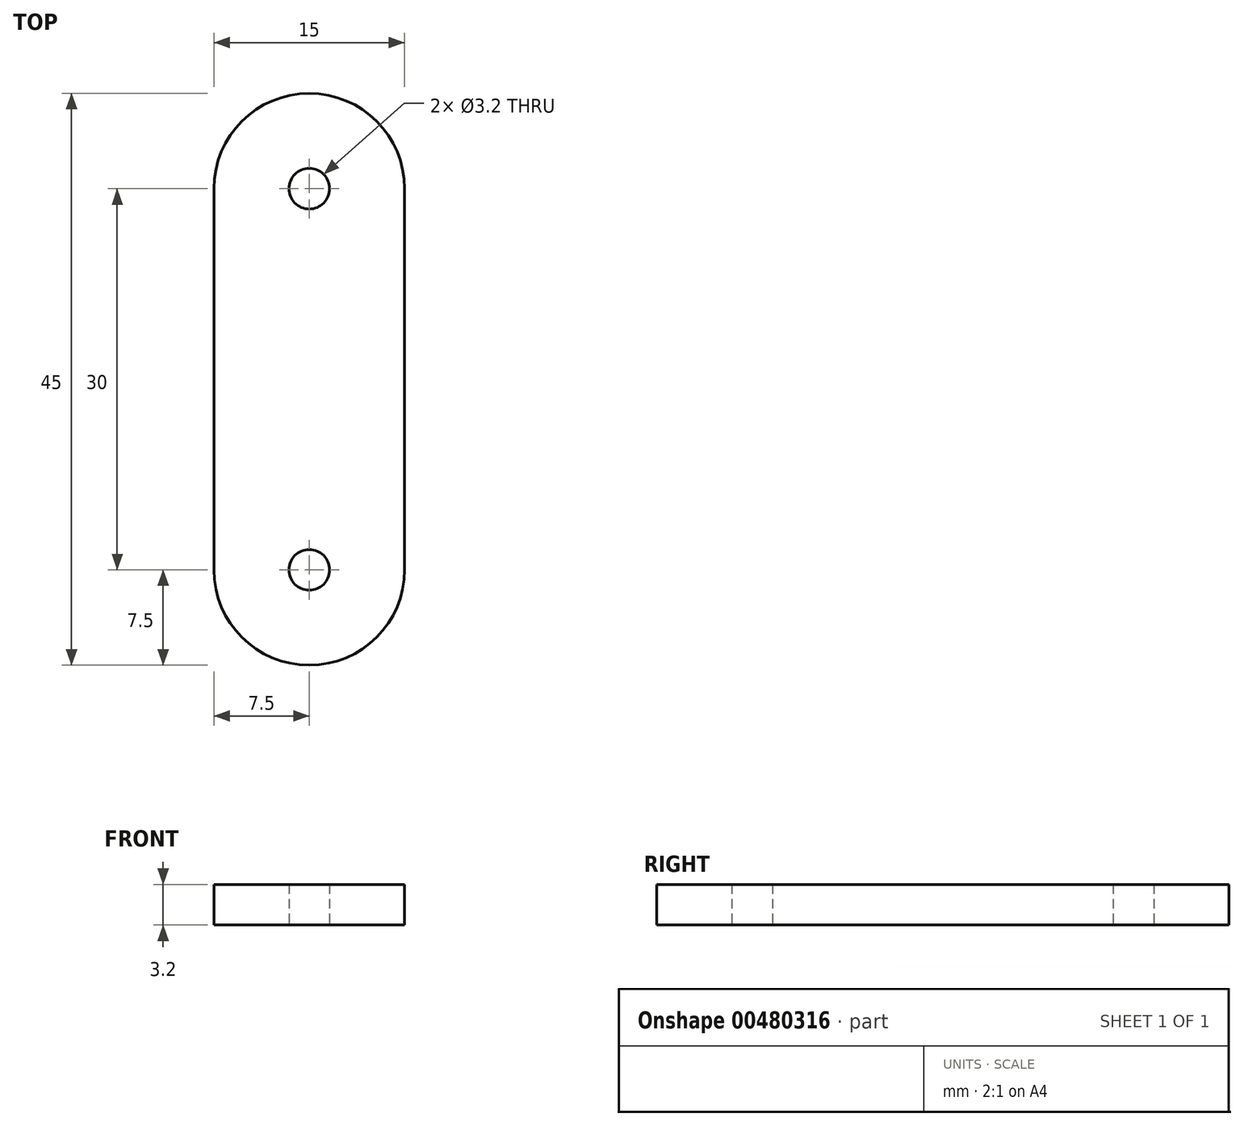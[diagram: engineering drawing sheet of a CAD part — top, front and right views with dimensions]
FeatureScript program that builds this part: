
annotation { "Feature Type Name" : "Feature", "Feature Type Description" : "" }
export const myFeature = defineFeature(function(context is Context, id is Id, definition is map)
    precondition{}
    {
        {
            var Q0;
            Q0=qCreatedBy(makeId("Top.planeOp"),FACE);
            var sketch = newSketch(context, id + "F0", { "sketchPlane" : qUnion([Q0])});
            skCircle(sketch, "E0", {"center": v(0, 0) * mm, "radius": 7.5 * mm});
            skLineSegment(sketch, "E1", {"start": v(0, 0) * mm, "end": v(0, 30) * mm, "construction": true});
            skCircle(sketch, "E2", {"center": v(0, 30) * mm, "radius": 7.5 * mm});
            skLineSegment(sketch, "E3", {"start": v(-7.5, 30) * mm, "end": v(-7.5, 0) * mm});
            skLineSegment(sketch, "E4", {"start": v(7.5, 30) * mm, "end": v(7.5, 0) * mm});
            skCircle(sketch, "E5", {"center": v(0, 30) * mm, "radius": 1.6 * mm});
            skCircle(sketch, "E6", {"center": v(0, 0) * mm, "radius": 1.6 * mm});
            skSolve(sketch);
        }
        {
            var Q0;
            Q0 = qSketchRegion(id + "F0", true);
            extrude(context, id + "F1", {"entities" : qUnion([Q0]), "depth" : 3.2 * mm});
        }
    });
